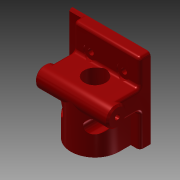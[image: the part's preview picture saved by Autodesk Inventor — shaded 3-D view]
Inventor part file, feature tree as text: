
AUTODESK INVENTOR PART (.ipt)
format: ipt  version: 2015 SP1 (Build 190203100, 203)  size: 302,080 bytes
history: native  units: in
note: dims shown in document units (in); Inventor stores cm internally (conversion verified against a paired STEP export)
features: sketch x8, reference x8, extrude x7, hole x2, plane x1, chamfer x1, fillet x1
ambient origin geometry x8: Origin, YZ Plane, XZ Plane, XY Plane, X Axis, Y Axis, Z Axis, Center Point
bodies: Solid1 (feature_tree)
feature tree (28):
  extrude  "Extrusion1"  Depth=1.1811in TaperAngle=0.0deg
  extrude  "Extrusion5"  Depth=0.7874in TaperAngle=0.0deg
  extrude  "Extrusion6"  Depth=0.0787in
  extrude  "Extrusion2"  Depth=0.0394in
  extrude  "Extrusion8"  Depth=0.2756in TaperAngle=0.0deg
  extrude  "Extrusion3"  Depth=0.0787in
  extrude  "Extrusion7"  Depth=0.0787in
  plane  "Work Plane1"
  hole  "Hole1"  [1 undecoded]
  hole  "Hole2"  [1 undecoded]
  chamfer  "Chamfer2"  Distance=0.2756in
  fillet  "Fillet3"  Radius=0.2756in
  sketch  "Sketch1"  dims[d0=1.5748in d1=1.1811in d2=0.0in]
  reference  "Reference1"
  reference  "Reference2"
  reference  "Reference3"
  reference  "Reference4"
  sketch  "Sketch2"  dims[d3=0.1181in d5=0.7874in d6=0.0in]
  sketch  "Sketch3"  dims[d7=0.0787in d8=0.0394in]
  sketch  "Sketch5"  dims[d9=0.0394in d10=0.0394in]
  sketch  "Sketch6"  dims[d11=0.0394in d12=0.2756in d13=0.0in]
  reference  "Reference6"
  sketch  "Sketch7"  dims[d14=0.0787in d15=0.4331in]
  sketch  "Sketch9"  dims[d19=0.0787in d20=0.0787in]
  reference  "Reference15"
  reference  "Reference16"
  reference  "Reference17"
  sketch  "Sketch10"  dims[d21=0.2756in d22=0.0in d23=0.5118in d24=0.5295in d25=0.2756in d26=0.0in d27=0.2756in d28=0.0in d30=0.1339in d31=0.276in d32=0.315in d33=0.8661in d34=90.0deg d35=0.315in d36=0.8108in d37=0.2362in d38=0.0968in d39=0.2362in d40=0.2559in d41=0.1181in d42=90.0deg d43=0.3465in d44=0.8108in d46=1.7323in d47=0.0in d49=0.7874in d53=0.0394in d54=0.0787in d55=45.0deg d56=0.0787in]
note: 2 required parameter values undecoded (feature->parameter linkage not recoverable at this tier; creation-order binding heuristic only, values carry confidence <= 0.55)
